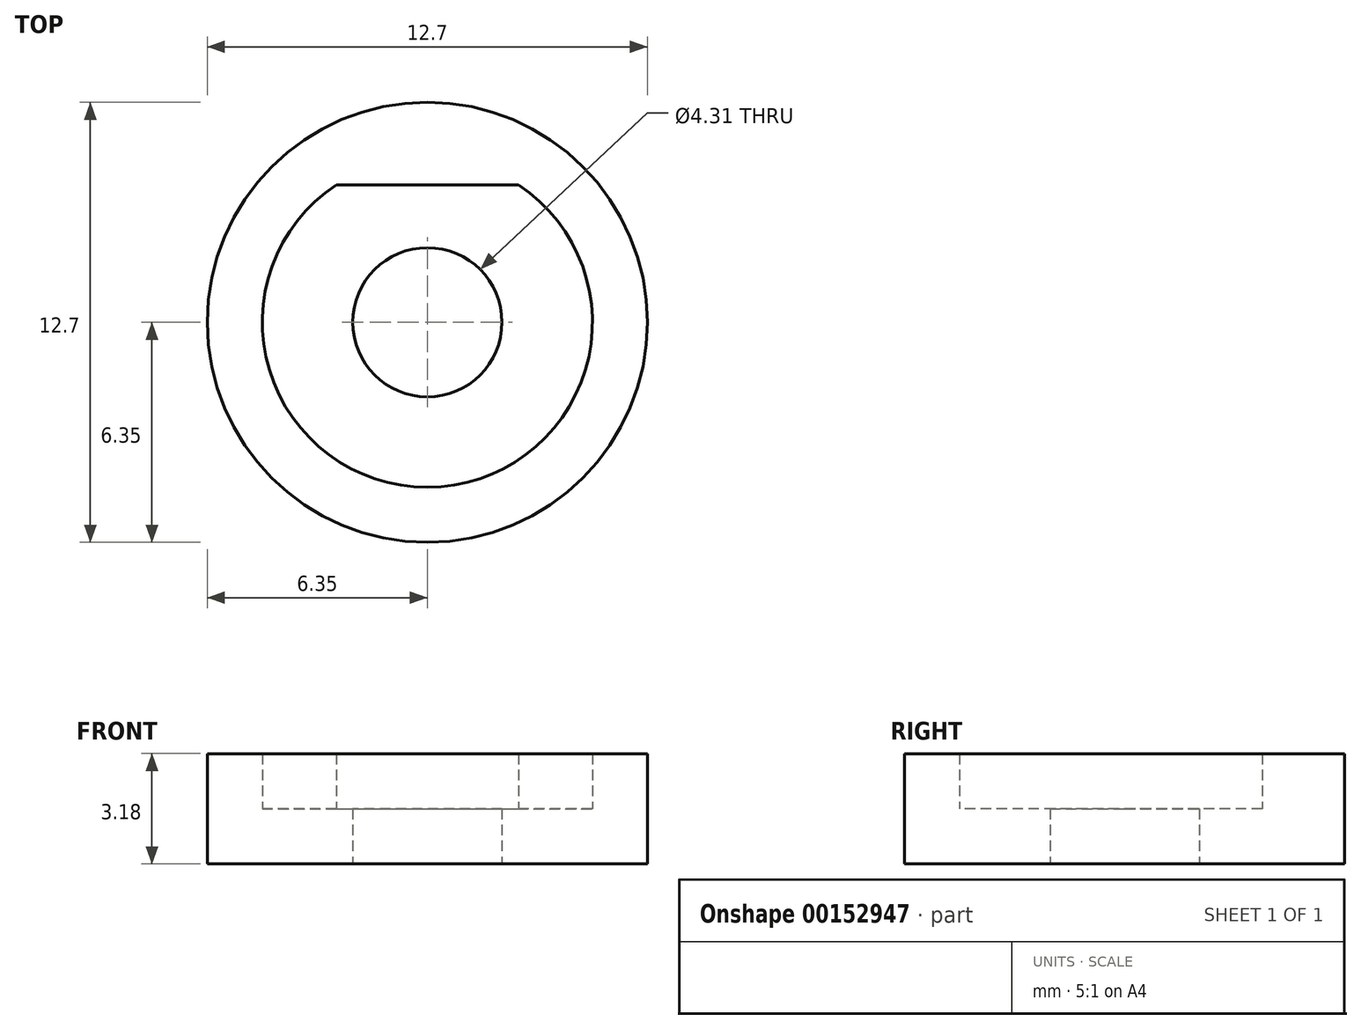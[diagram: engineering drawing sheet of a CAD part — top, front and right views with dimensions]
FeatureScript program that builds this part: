
annotation { "Feature Type Name" : "Feature", "Feature Type Description" : "" }
export const myFeature = defineFeature(function(context is Context, id is Id, definition is map)
    precondition{}
    {
        {
            var Q0;
            Q0=qCreatedBy(makeId("Top.planeOp"),FACE);
            var sketch = newSketch(context, id + "F0", { "sketchPlane" : qUnion([Q0])});
            skCircle(sketch, "E0", {"center": v(0, 0) * mm, "radius": 6.35 * mm});
            skCircle(sketch, "E1", {"center": v(0, 0) * mm, "radius": 2.15 * mm});
            skSolve(sketch);
        }
        {
            var Q0;
            Q0 = qSketchRegion(id + "F0", true);
            extrude(context, id + "F1", {"entities" : qUnion([Q0]), "depth" : 1.59 * mm});
        }
        {
            var Q0;
            Q0=makeQuery(id+"F1.opExtrude","CAP_FACE",FACE,{"disambiguationData":[OSD([sQuery(id+"F0.wireOp",EDGE,"E0"),sQuery(id+"F0.wireOp",EDGE,"E1")])],"isStart":false});
            var sketch = newSketch(context, id + "F2", { "sketchPlane" : qUnion([Q0])});
            skArc(sketch, "E2", {"start": v(-2.63, 3.97) * mm, "mid": v(0, -4.76) * mm, "end": v(2.63, 3.97) * mm});
            skLineSegment(sketch, "E3", {"start": v(-2.63, 3.97) * mm, "end": v(2.63, 3.97) * mm});
            skLineSegment(sketch, "E4", {"start": v(0, 0) * mm, "end": v(0, 3.97) * mm, "construction": true});
            skCircle(sketch, "E5", {"center": v(0, 0) * mm, "radius": 6.35 * mm});
            skSolve(sketch);
        }
        {
            var Q0;
            Q0 = qSketchRegion(id + "F2", true);
            extrude(context, id + "F3", {"entities" : qUnion([Q0]), "operationType" : NewBodyOperationType.ADD, "depth" : 1.59 * mm});
        }
    });
